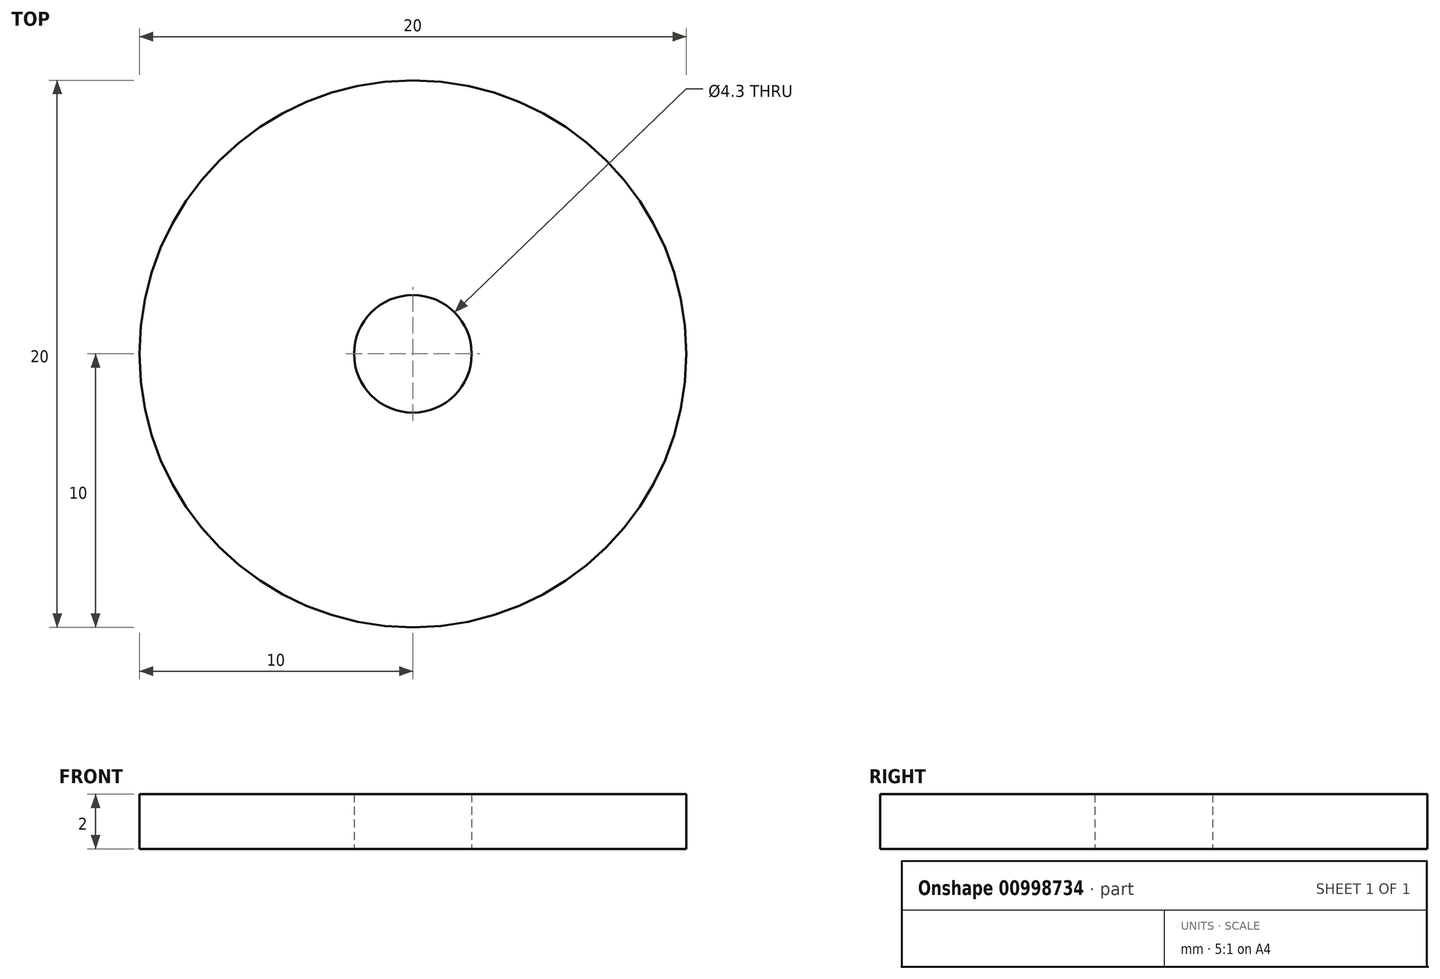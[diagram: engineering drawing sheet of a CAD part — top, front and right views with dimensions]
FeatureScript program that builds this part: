
annotation { "Feature Type Name" : "Feature", "Feature Type Description" : "" }
export const myFeature = defineFeature(function(context is Context, id is Id, definition is map)
    precondition{}
    {
        {
            var Q0;
            Q0=qCreatedBy(makeId("Top.planeOp"),FACE);
            var sketch = newSketch(context, id + "F0", { "sketchPlane" : qUnion([Q0])});
            skCircle(sketch, "E0", {"center": v(0, 0) * mm, "radius": 2.15 * mm});
            skCircle(sketch, "E1", {"center": v(0, 0) * mm, "radius": 10 * mm});
            skSolve(sketch);
        }
        {
            var Q0;
            Q0 = qSketchRegion(id + "F0", true);
            extrude(context, id + "F1", {"entities" : qUnion([Q0]), "depth" : 2 * mm, "offsetDistance" : 25 * mm});
        }
    });
